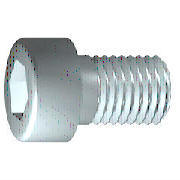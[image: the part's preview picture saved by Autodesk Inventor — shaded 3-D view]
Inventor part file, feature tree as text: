
AUTODESK INVENTOR PART (.ipt)
format: ipt  version: 2020 (Build 240168000, 168)  size: 194,048 bytes
history: native  units: mm (DEFAULTED — no unit token found)
features: sketch x2, other x1, extrude x1, plane x1, fillet x1
ambient origin geometry x7: Origin, YZ Plane, XY Plane, X Axis, Y Axis, Z Axis, Center Point
bodies: Solid1 (feature_tree)
feature tree (6):
  other  "Bryła"
  extrude  "Szczelina"  Depth=22.0mm
  plane  "Work Plane1"
  fillet  "Fillet2"  Radius=0.61355mm
  sketch  "Szkic1"
  sketch  "Szkic2"
